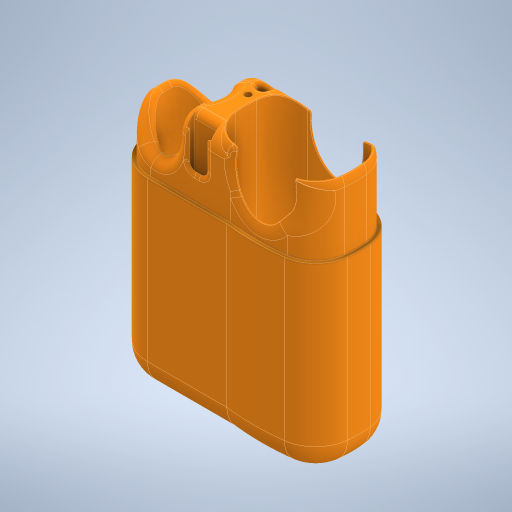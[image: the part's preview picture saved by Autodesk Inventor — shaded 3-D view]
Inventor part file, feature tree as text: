
AUTODESK INVENTOR PART (.ipt)
format: ipt  version: 2023 (Build 270158030, 158C)  size: 1,760,256 bytes
history: native  units: mm
features: fillet x17, extrude x16, sketch x16, projected_geometry x7, other x4, plane x1
ambient origin geometry x8: Origin, YZ Plane, XZ Plane, XY Plane, X Axis, Y Axis, Z Axis, Center Point
bodies: Body1 (feature_tree), Body2 (feature_tree), Body3 (feature_tree), Body4 (feature_tree)
feature tree (61):
  other  "vape"
  extrude  "Extrusion1"  Depth=8.35mm
  fillet  "Fillet1"  Radius=70.0mm
  extrude  "Extrusion2"  Depth=11.6mm TaperAngle=0.0deg
  plane  "Work Plane1"
  extrude  "Extrusion3"  Depth=45.8mm TaperAngle=0.0deg
  extrude  "Extrusion4"  Depth=22.1mm
  extrude  "Extrusion5"  Depth=1.5mm
  extrude  "Extrusion6"  Depth=1.5mm
  fillet  "Fillet2"  Radius=1.5mm
  extrude  "Extrusion7"  Depth=15.55mm
  extrude  "Extrusion8"  Depth=3.0mm
  fillet  "Fillet3"  Radius=3.0mm
  fillet  "Fillet4"  Radius=3.0mm
  extrude  "Extrusion9"  Depth=15.55mm
  fillet  "Fillet5"  Radius=2.0mm
  fillet  "Fillet6"  Radius=13.0mm
  fillet  "Fillet9"  Radius=2.0mm
  extrude  "Extrusion10"  Depth=11.0mm
  extrude  "Extrusion11"  Depth=20.0mm TaperAngle=0.0deg
  fillet  "Fillet10"  Radius=4.0mm
  extrude  "Extrusion13"  Depth=8.0mm
  extrude  "Extrusion14"  Depth=10.0mm
  extrude  "Extrusion15"  Depth=17.0mm
  fillet  "Fillet13"  [1 undecoded]
  fillet  "Fillet14"  Radius=8.0mm
  extrude  "Extrusion16"  Depth=10.0mm
  fillet  "Fillet15"  Radius=6.0mm
  fillet  "Fillet16"  Radius=3.0mm
  fillet  "Fillet17"  Radius=2.9mm
  fillet  "Fillet18"  Radius=5.0mm
  fillet  "Fillet19"  Radius=24.5mm
  extrude  "Extrusion17"  Depth=62.0mm TaperAngle=0.0deg
  fillet  "Fillet20"  Radius=2.4mm
  fillet  "Fillet21"  Radius=7.3mm
  sketch  "Sketch1"  dims[d4=98.5mm d5=0.0mm d9=8.35mm d22=70.0mm d23=0.0mm]
  sketch  "Sketch2"  dims[d24=20.0mm d26=11.6mm d27=0.0mm]
  other  "vape-tube"
  sketch  "Sketch3"  dims[d28=16.0mm d29=45.8mm d30=0.0mm]
  other  "storage"
  sketch  "Sketch4"  dims[d31=16.0mm d38=22.1mm]
  sketch  "Sketch5"  dims[d39=31.1mm d41=1.5mm]
  projected_geometry  "Projected Loop2"
  sketch  "Sketch6"  dims[d42=1.5mm d44=1.5mm d45=1.5mm]
  projected_geometry  "Projected Loop3"
  projected_geometry  "Projected Loop4"
  sketch  "Sketch7"  dims[d46=11.05mm d47=15.55mm]
  projected_geometry  "Projected Loop5"
  sketch  "Sketch8"  dims[d48=3.0mm d49=3.0mm d50=3.0mm d51=3.0mm]
  projected_geometry  "Projected Loop6"
  sketch  "Sketch9"  dims[d52=11.05mm d53=15.55mm d54=2.0mm d55=13.0mm]
  sketch  "Sketch10"  dims[d56=12.5mm d57=60.0mm d58=0.0mm d59=2.0mm]
  sketch  "Sketch11"  dims[d60=10.0mm d61=0.0mm d62=11.0mm]
  sketch  "Sketch13"  dims[d63=1.0mm d64=20.0mm d65=0.0mm d66=4.0mm d67=0.0mm]
  sketch  "Sketch14"  dims[d68=5.0mm d69=8.0mm]
  projected_geometry  "Projected Loop7"
  sketch  "Sketch15"  dims[d70=0.0mm d71=10.0mm]
  projected_geometry  "Projected Loop8"
  other  "vape-lid"
  sketch  "Sketch16"  dims[d72=7.0mm d73=17.0mm d74=0.0mm d75=0.0mm d76=8.0mm]
  sketch  "Sketch17"  dims[d77=2.0mm d80=10.0mm d81=6.0mm d82=3.0mm d83=2.9mm d84=5.0mm d85=24.5mm d86=62.0mm d87=0.0mm d88=2.4mm d89=7.3mm d90=0.5mm d91=8.7mm d92=36.0mm d93=0.0mm d94=1.0mm d103=2.0mm d104=3.0mm d105=71.0mm d106=0.0mm d107=0.05mm d108=71.0mm d109=0.0mm d110=3.0mm d111=30.0deg d112=1.5mm d113=1.5mm d114=1.0mm d115=1.0mm d116=10.0mm d117=10.0mm d118=0.0mm d119=2.0mm d120=2.0mm d121=0.2mm d122=0.2mm d123=0.2mm d124=16.0mm d125=6.0mm d126=10.0mm d127=0.0mm d128=6.8mm d129=2.0mm d130=0.2mm d131=1.0mm]
note: 1 required parameter value undecoded (feature->parameter linkage not recoverable at this tier; creation-order binding heuristic only, values carry confidence <= 0.55)
